# Revit family: NLRS_57_DUA_FB_inspection-panal-round-duct_LT_velu
name_source: partatom
category: Duct Accessories
units: mm (PartAtom-declared; Revit-internal decimal feet)

## family parameters
Cut with Voids When Loaded = No
Host = Face
Part Type = Attaches To
Round Connector Dimension = Use Diameter
Shared = No

## types (10) — shared parameters
Assembly Code = 57.00
Description = Inspectiedeksel voor rond kanaal
Manufacturer = Velu Klimaattechnische groothandel
NLRS_C_content_datum_gewijzigd = 21-11-2023
NLRS_C_content_provider = Velu Klimaattechnische groothandel
NLRS_C_content_versie = 3.21.01
NLRS_C_description = Inspectiedeksel voor rond kanaal
Type Comments = Face Based
URL = https://webshop.velu.nl
VELU_Article_Data = VID

## per-type parameters (varying)
| type | Default Elevation | Model | VELU_Calculation_Parameter | VELU_Calculation_Parameter2 | VELU_Model | VELU_Model_Radius | VELU_Model_Radius2 | VELU_Model_Radius3 | VELU_Zoek_Dia1 |
| VID 100 | 1219 mm | VID 100 180x80 | 80 mm  [stored 0.262467 ft] | 180 mm  [stored 0.590551 ft] | VID 100 180x80 | 50 mm  [stored 0.164042 ft] | 49 mm  [stored 0.160761 ft] | 41 mm  [stored 0.134514 ft] | 100 mm  [stored 0.328084 ft] |
| VID 125 | 1219 mm | VID 125 180x80 | 80 mm  [stored 0.262467 ft] | 180 mm  [stored 0.590551 ft] | VID 125 180x80 | 63 mm | 62 mm | 41 mm  [stored 0.134514 ft] | 125 mm  [stored 0.410105 ft] |
| VID 150 | 1219 mm | VID 150 200x100 | 100 mm  [stored 0.328084 ft] | 200 mm  [stored 0.656168 ft] | VID 150 200x100 | 75 mm | 74 mm  [stored 0.242782 ft] | 51 mm | 150 mm  [stored 0.492126 ft] |
| VID 160 | 1219 mm | VID 160 200x100 | 100 mm  [stored 0.328084 ft] | 200 mm  [stored 0.656168 ft] | VID 160 200x100 | 80 mm  [stored 0.262467 ft] | 79 mm | 51 mm | 160 mm  [stored 0.524934 ft] |
| VID 200 | 0 mm  [stored 0 ft] | VID 200 200x100 | 100 mm  [stored 0.328084 ft] | 200 mm  [stored 0.656168 ft] | VID 200 200x100 | 100 mm  [stored 0.328084 ft] | 99 mm  [stored 0.324803 ft] | 51 mm | 200 mm  [stored 0.656168 ft] |
| VID 250 | 1219 mm | VID 250 200x100 | 100 mm  [stored 0.328084 ft] | 200 mm  [stored 0.656168 ft] | VID 250 200x100 | 125 mm  [stored 0.410105 ft] | 124 mm  [stored 0.406824 ft] | 51 mm | 250 mm  [stored 0.82021 ft] |
| VID 315 | 1219 mm | VID 315 300x200 | 200 mm  [stored 0.656168 ft] | 300 mm  [stored 0.984252 ft] | VID 315 300x200 | 158 mm | 157 mm | 101 mm  [stored 0.331365 ft] | 315 mm  [stored 1.03346 ft] |
| VID 400 | 1219 mm | VID 400 400x300 | 300 mm  [stored 0.984252 ft] | 400 mm  [stored 1.31234 ft] | VID 400 400x300 | 200 mm  [stored 0.656168 ft] | 199 mm  [stored 0.652887 ft] | 151 mm  [stored 0.495407 ft] | 400 mm  [stored 1.31234 ft] |
| VID 500 | 1219 mm | VID 500 400x300 | 300 mm  [stored 0.984252 ft] | 400 mm  [stored 1.31234 ft] | VID 500 400x300 | 250 mm  [stored 0.82021 ft] | 249 mm  [stored 0.816929 ft] | 151 mm  [stored 0.495407 ft] | 500 mm  [stored 1.64042 ft] |
| VID 630 | 1219 mm | VID 630 400x300 | 300 mm  [stored 0.984252 ft] | 400 mm  [stored 1.31234 ft] | VID 630 400x300 | 315 mm  [stored 1.03346 ft] | 314 mm  [stored 1.03018 ft] | 151 mm  [stored 0.495407 ft] | 630 mm  [stored 2.06693 ft] |

note: [stored X ft] marks values corroborated as IEEE doubles in the binary element streams (Revit-internal decimal feet)

## geometry (parser evidence)
native form markers: Sweep x3
no freeform markers — native parametric forms only
